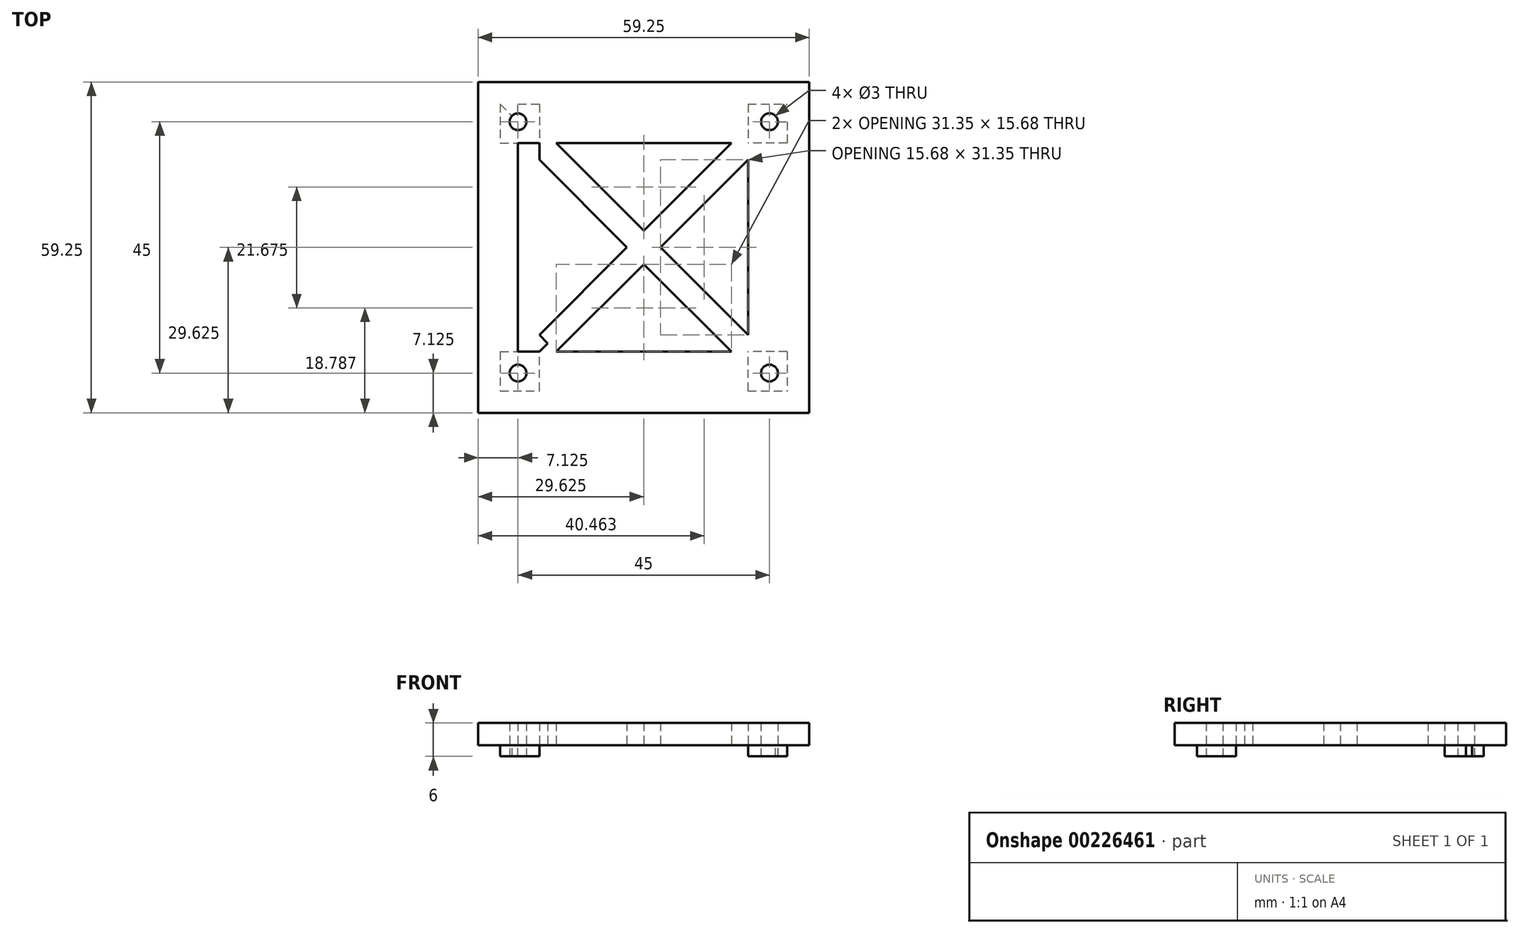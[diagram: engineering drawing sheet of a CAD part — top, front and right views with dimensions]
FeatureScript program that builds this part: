
annotation { "Feature Type Name" : "Feature", "Feature Type Description" : "" }
export const myFeature = defineFeature(function(context is Context, id is Id, definition is map)
    precondition{}
    {
        {
            var Q0;
            Q0=qCreatedBy(makeId("Top.planeOp"),FACE);
            var sketch = newSketch(context, id + "F0", { "sketchPlane" : qUnion([Q0])});
            skLineSegment(sketch, "E0.bottom", {"start": v(0, 0) * mm, "end": v(51.35, 0) * mm});
            skLineSegment(sketch, "E0.top", {"start": v(0, -51.35) * mm, "end": v(51.35, -51.35) * mm});
            skLineSegment(sketch, "E0.left", {"start": v(0, 0) * mm, "end": v(0, -51.35) * mm});
            skLineSegment(sketch, "E0.right", {"start": v(51.35, 0) * mm, "end": v(51.35, -51.35) * mm});
            skCircle(sketch, "E1", {"center": v(3.17, -3.17) * mm, "radius": 1.5 * mm});
            skCircle(sketch, "E2", {"center": v(48.17, -3.18) * mm, "radius": 1.5 * mm});
            skCircle(sketch, "E3", {"center": v(48.18, -48.17) * mm, "radius": 1.5 * mm});
            skCircle(sketch, "E4", {"center": v(3.18, -48.17) * mm, "radius": 1.5 * mm});
            skLineSegment(sketch, "E5", {"start": v(3.18, -51.35) * mm, "end": v(3.18, -48.17) * mm});
            skLineSegment(sketch, "E6", {"start": v(3.18, -48.17) * mm, "end": v(0, -48.17) * mm});
            skLineSegment(sketch, "E7", {"start": v(48.18, -48.17) * mm, "end": v(51.35, -48.17) * mm});
            skLineSegment(sketch, "E8", {"start": v(48.18, -48.17) * mm, "end": v(48.18, -51.35) * mm});
            skLineSegment(sketch, "E9", {"start": v(48.17, -3.18) * mm, "end": v(48.17, 0) * mm});
            skLineSegment(sketch, "E10", {"start": v(0, 0) * mm, "end": v(0, 0) * mm});
            skLineSegment(sketch, "E11", {"start": v(0, 0) * mm, "end": v(-3.95, 3.95) * mm});
            skLineSegment(sketch, "E12", {"start": v(51.35, 0) * mm, "end": v(55.3, 3.95) * mm});
            skLineSegment(sketch, "E13", {"start": v(51.35, -51.35) * mm, "end": v(55.3, -55.3) * mm});
            skLineSegment(sketch, "E14", {"start": v(55.3, -55.3) * mm, "end": v(-3.95, -55.3) * mm});
            skLineSegment(sketch, "E15", {"start": v(-3.95, -55.3) * mm, "end": v(0, -51.35) * mm});
            skLineSegment(sketch, "E16", {"start": v(-3.95, -55.3) * mm, "end": v(-3.95, 3.95) * mm});
            skLineSegment(sketch, "E17", {"start": v(55.3, 3.95) * mm, "end": v(-3.95, 3.95) * mm});
            skLineSegment(sketch, "E18", {"start": v(55.3, 3.95) * mm, "end": v(55.3, -55.3) * mm});
            skLineSegment(sketch, "E19.bottom", {"start": v(0, -51.35) * mm, "end": v(7, -51.35) * mm});
            skLineSegment(sketch, "E19.top", {"start": v(0, -44.35) * mm, "end": v(7, -44.35) * mm});
            skLineSegment(sketch, "E19.left", {"start": v(0, -51.35) * mm, "end": v(0, -44.35) * mm});
            skLineSegment(sketch, "E19.right", {"start": v(7, -51.35) * mm, "end": v(7, -44.35) * mm});
            skLineSegment(sketch, "E20.bottom", {"start": v(51.35, -51.35) * mm, "end": v(44.35, -51.35) * mm});
            skLineSegment(sketch, "E20.top", {"start": v(51.35, -44.35) * mm, "end": v(44.35, -44.35) * mm});
            skLineSegment(sketch, "E20.left", {"start": v(51.35, -51.35) * mm, "end": v(51.35, -44.35) * mm});
            skLineSegment(sketch, "E20.right", {"start": v(44.35, -51.35) * mm, "end": v(44.35, -44.35) * mm});
            skLineSegment(sketch, "E21.bottom", {"start": v(51.35, 0) * mm, "end": v(44.35, 0) * mm});
            skLineSegment(sketch, "E21.top", {"start": v(51.35, -7) * mm, "end": v(44.35, -7) * mm});
            skLineSegment(sketch, "E21.left", {"start": v(51.35, 0) * mm, "end": v(51.35, -7) * mm});
            skLineSegment(sketch, "E21.right", {"start": v(44.35, 0) * mm, "end": v(44.35, -7) * mm});
            skLineSegment(sketch, "E22.bottom", {"start": v(0, 0) * mm, "end": v(7, 0) * mm});
            skLineSegment(sketch, "E22.top", {"start": v(0, -7) * mm, "end": v(7, -7) * mm});
            skLineSegment(sketch, "E22.left", {"start": v(0, 0) * mm, "end": v(0, -7) * mm});
            skLineSegment(sketch, "E22.right", {"start": v(7, 0) * mm, "end": v(7, -7) * mm});
            skLineSegment(sketch, "E23", {"start": v(7, -44.35) * mm, "end": v(7, -7) * mm});
            skLineSegment(sketch, "E24", {"start": v(44.35, -7) * mm, "end": v(7, -7) * mm});
            skLineSegment(sketch, "E25", {"start": v(44.35, -7) * mm, "end": v(44.35, -44.35) * mm});
            skLineSegment(sketch, "E26", {"start": v(44.35, -44.35) * mm, "end": v(7, -44.35) * mm});
            skLineSegment(sketch, "E27", {"start": v(7, -44.35) * mm, "end": v(44.35, -7) * mm});
            skLineSegment(sketch, "E28", {"start": v(44.35, -44.35) * mm, "end": v(7, -7) * mm});
            skLineSegment(sketch, "E29", {"start": v(10, -44.35) * mm, "end": v(44.35, -10) * mm});
            skLineSegment(sketch, "E30", {"start": v(44.35, -10) * mm, "end": v(41.35, -7) * mm});
            skLineSegment(sketch, "E31", {"start": v(41.35, -7) * mm, "end": v(7, -41.35) * mm});
            skLineSegment(sketch, "E32", {"start": v(7, -10) * mm, "end": v(41.35, -44.35) * mm});
            skLineSegment(sketch, "E33", {"start": v(41.35, -44.35) * mm, "end": v(44.35, -41.35) * mm});
            skLineSegment(sketch, "E34", {"start": v(44.35, -41.35) * mm, "end": v(10, -7) * mm});
            skLineSegment(sketch, "E35", {"start": v(10, -7) * mm, "end": v(7, -10) * mm});
            skLineSegment(sketch, "E36", {"start": v(7, -41.35) * mm, "end": v(10, -44.35) * mm});
            skLineSegment(sketch, "E37", {"start": v(42.85, -8.5) * mm, "end": v(41.35, -7) * mm});
            skLineSegment(sketch, "E38", {"start": v(7, -41.35) * mm, "end": v(7, -44.35) * mm});
            skLineSegment(sketch, "E39", {"start": v(0, -51.35) * mm, "end": v(7, -44.35) * mm});
            skLineSegment(sketch, "E40", {"start": v(0, 0) * mm, "end": v(7, -7) * mm});
            skLineSegment(sketch, "E41", {"start": v(51.35, 0) * mm, "end": v(44.35, -7) * mm});
            skLineSegment(sketch, "E42", {"start": v(44.35, -44.35) * mm, "end": v(51.35, -51.35) * mm});
            skLineSegment(sketch, "E43", {"start": v(48.17, -3.18) * mm, "end": v(51.35, -3.18) * mm});
            skLineSegment(sketch, "E44", {"start": v(3.17, -3.17) * mm, "end": v(0, -3.17) * mm});
            skLineSegment(sketch, "E45", {"start": v(3.17, -3.17) * mm, "end": v(3.17, 0) * mm});
            skLineSegment(sketch, "E46", {"start": v(3.18, -48.17) * mm, "end": v(48.18, -48.17) * mm});
            skLineSegment(sketch, "E47", {"start": v(48.17, -48.17) * mm, "end": v(48.17, -3.18) * mm});
            skLineSegment(sketch, "E48", {"start": v(48.17, -3.18) * mm, "end": v(3.18, -3.17) * mm});
            skLineSegment(sketch, "E49", {"start": v(3.17, -3.18) * mm, "end": v(3.18, -48.17) * mm});
            skSolve(sketch);
        }
        {
            var Q0;
            {var subQ2=sQuery(id+"F0.wireOp",EDGE,"E0.top");Q0=makeQuery(id+"F0.imprint","IMPRINT",FACE,{"disambiguationData":[TD([[makeQuery(id+"F0.imprint","IMPRINT",EDGE,{"derivedFrom":subQ2}),-1.0]])]});}
            var Q1;
            Q1=makeQuery(id+"F0.imprint","IMPRINT",FACE,{"disambiguationData":[TD([[makeQuery(id+"F0.imprint","IMPRINT",EDGE,{"derivedFrom":sQuery(id+"F0.wireOp",EDGE,"E0.left")}),1.0]])]});
            var Q2;
            Q2=makeQuery(id+"F0.imprint","IMPRINT",FACE,{"disambiguationData":[TD([[makeQuery(id+"F0.imprint","IMPRINT",EDGE,{"derivedFrom":sQuery(id+"F0.wireOp",EDGE,"E0.top")}),1.0]])]});
            var Q3;
            {var subQ9=sQuery(id+"F0.wireOp",EDGE,"E19.top");Q3=makeQuery(id+"F0.imprint","IMPRINT",FACE,{"disambiguationData":[TD([[makeQuery(id+"F0.imprint","IMPRINT",EDGE,{"derivedFrom":subQ9}),-1.0]])]});}
            var Q4;
            {var subQ1=sQuery(id+"F0.wireOp",EDGE,"E5");var subQ7=sQuery(id+"F0.wireOp",EDGE,"E4");var subQ9=makeQuery(id+"F0.imprint","INTERSECT",VERTEX,{"derivedFrom":[subQ7,subQ1]});Q4=makeQuery(id+"F0.imprint","IMPRINT",FACE,{"disambiguationData":[TD([[makeQuery(id+"F0.imprint","IMPRINT",EDGE,{"disambiguationData":[TD([[subQ9,1.0]])],"derivedFrom":subQ7}),-1.0]])]});}
            var Q5;
            {var subQ1=sQuery(id+"F0.wireOp",EDGE,"E0.left");Q5=makeQuery(id+"F0.imprint","IMPRINT",FACE,{"disambiguationData":[TD([[makeQuery(id+"F0.imprint","IMPRINT",EDGE,{"derivedFrom":subQ1}),-1.0]])]});}
            var Q6;
            {var subQ4=sQuery(id+"F0.wireOp",EDGE,"Czqd3Wxc-25fJ-mDIk-frtU-pVyHBjyavdYw");Q6=makeQuery(id+"F0.imprint","IMPRINT",FACE,{"disambiguationData":[TD([[makeQuery(id+"F0.imprint","IMPRINT",EDGE,{"derivedFrom":subQ4}),-1.0]])]});}
            var Q7;
            {var subQ0=sQuery(id+"F0.wireOp",EDGE,"nTWrYmdF-bnnp-oIgE-1onG-Oaq0rmlScgZV");Q7=makeQuery(id+"F0.imprint","IMPRINT",FACE,{"disambiguationData":[TD([[makeQuery(id+"F0.imprint","IMPRINT",EDGE,{"derivedFrom":subQ0}),1.0]])]});}
            var Q8;
            {var subQ0=sQuery(id+"F0.wireOp",EDGE,"Czqd3Wxc-25fJ-mDIk-frtU-pVyHBjyavdYw");Q8=makeQuery(id+"F0.imprint","IMPRINT",FACE,{"disambiguationData":[TD([[makeQuery(id+"F0.imprint","IMPRINT",EDGE,{"derivedFrom":subQ0}),1.0]])]});}
            var Q9;
            {var subQ2=sQuery(id+"F0.wireOp",EDGE,"E0.bottom");Q9=makeQuery(id+"F0.imprint","IMPRINT",FACE,{"disambiguationData":[TD([[makeQuery(id+"F0.imprint","IMPRINT",EDGE,{"derivedFrom":subQ2}),1.0]])]});}
            var Q10;
            Q10=makeQuery(id+"F0.imprint","IMPRINT",FACE,{"disambiguationData":[TD([[makeQuery(id+"F0.imprint","IMPRINT",EDGE,{"derivedFrom":sQuery(id+"F0.wireOp",EDGE,"E0.bottom")}),-1.0]])]});
            var Q11;
            {var subQ4=sQuery(id+"F0.wireOp",EDGE,"JuPnyzvd-dEvb-ISZh-nlHp-12VVDodoZXJM");Q11=makeQuery(id+"F0.imprint","IMPRINT",FACE,{"disambiguationData":[TD([[makeQuery(id+"F0.imprint","IMPRINT",EDGE,{"derivedFrom":subQ4}),1.0]])]});}
            var Q12;
            {var subQ5=sQuery(id+"F0.wireOp",EDGE,"JuPnyzvd-dEvb-ISZh-nlHp-12VVDodoZXJM");Q12=makeQuery(id+"F0.imprint","IMPRINT",FACE,{"disambiguationData":[TD([[makeQuery(id+"F0.imprint","IMPRINT",EDGE,{"derivedFrom":subQ5}),-1.0]])]});}
            var Q13;
            {var subQ4=sQuery(id+"F0.wireOp",EDGE,"E0.right");Q13=makeQuery(id+"F0.imprint","IMPRINT",FACE,{"disambiguationData":[TD([[makeQuery(id+"F0.imprint","IMPRINT",EDGE,{"derivedFrom":subQ4}),1.0]])]});}
            var Q14;
            Q14=makeQuery(id+"F0.imprint","IMPRINT",FACE,{"disambiguationData":[TD([[makeQuery(id+"F0.imprint","IMPRINT",EDGE,{"derivedFrom":sQuery(id+"F0.wireOp",EDGE,"E0.right")}),-1.0]])]});
            var Q15;
            {var subQ3=sQuery(id+"F0.wireOp",EDGE,"E3");var subQ7=sQuery(id+"F0.wireOp",EDGE,"E7");var subQ9=makeQuery(id+"F0.imprint","INTERSECT",VERTEX,{"derivedFrom":[subQ3,subQ7]});Q15=makeQuery(id+"F0.imprint","IMPRINT",FACE,{"disambiguationData":[TD([[makeQuery(id+"F0.imprint","IMPRINT",EDGE,{"disambiguationData":[TD([[subQ9,1.0]])],"derivedFrom":subQ3}),-1.0]])]});}
            var Q16;
            {var subQ10=sQuery(id+"F0.wireOp",EDGE,"E20.top");Q16=makeQuery(id+"F0.imprint","IMPRINT",FACE,{"disambiguationData":[TD([[makeQuery(id+"F0.imprint","IMPRINT",EDGE,{"derivedFrom":subQ10}),1.0]])]});}
            var Q17;
            {var subQ0=sQuery(id+"F0.wireOp",EDGE,"E38");Q17=makeQuery(id+"F0.imprint","IMPRINT",FACE,{"disambiguationData":[TD([[makeQuery(id+"F0.imprint","IMPRINT",EDGE,{"derivedFrom":subQ0}),1.0]])]});}
            var Q18;
            {var subQ0=sQuery(id+"F0.wireOp",EDGE,"E27");var subQ3=sQuery(id+"F0.wireOp",EDGE,"E36");var subQ5=makeQuery(id+"F0.imprint","INTERSECT",VERTEX,{"derivedFrom":[subQ0,subQ3]});Q18=makeQuery(id+"F0.imprint","IMPRINT",FACE,{"disambiguationData":[TD([[makeQuery(id+"F0.imprint","IMPRINT",EDGE,{"disambiguationData":[TD([[subQ5,-1.0]])],"derivedFrom":subQ3}),-1.0]])]});}
            var Q19;
            {var subQ0=sQuery(id+"F0.wireOp",EDGE,"E36");var subQ1=sQuery(id+"F0.wireOp",EDGE,"E27");var subQ2=makeQuery(id+"F0.imprint","INTERSECT",VERTEX,{"derivedFrom":[subQ1,subQ0]});Q19=makeQuery(id+"F0.imprint","IMPRINT",FACE,{"disambiguationData":[TD([[makeQuery(id+"F0.imprint","IMPRINT",EDGE,{"disambiguationData":[TD([[subQ2,-1.0]])],"derivedFrom":subQ1}),-1.0]])]});}
            var Q20;
            {var subQ0=sQuery(id+"F0.wireOp",EDGE,"E36");var subQ1=sQuery(id+"F0.wireOp",EDGE,"E27");var subQ2=makeQuery(id+"F0.imprint","INTERSECT",VERTEX,{"derivedFrom":[subQ1,subQ0]});Q20=makeQuery(id+"F0.imprint","IMPRINT",FACE,{"disambiguationData":[TD([[makeQuery(id+"F0.imprint","IMPRINT",EDGE,{"disambiguationData":[TD([[subQ2,-1.0]])],"derivedFrom":subQ1}),1.0]])]});}
            var Q21;
            {var subQ0=sQuery(id+"F0.wireOp",EDGE,"E31");var subQ1=sQuery(id+"F0.wireOp",EDGE,"E28");var subQ2=makeQuery(id+"F0.imprint","INTERSECT",VERTEX,{"derivedFrom":[subQ1,subQ0]});Q21=makeQuery(id+"F0.imprint","IMPRINT",FACE,{"disambiguationData":[TD([[makeQuery(id+"F0.imprint","IMPRINT",EDGE,{"disambiguationData":[TD([[subQ2,-1.0]])],"derivedFrom":subQ1}),1.0]])]});}
            var Q22;
            {var subQ0=sQuery(id+"F0.wireOp",EDGE,"E31");var subQ1=sQuery(id+"F0.wireOp",EDGE,"E28");var subQ2=makeQuery(id+"F0.imprint","INTERSECT",VERTEX,{"derivedFrom":[subQ1,subQ0]});Q22=makeQuery(id+"F0.imprint","IMPRINT",FACE,{"disambiguationData":[TD([[makeQuery(id+"F0.imprint","IMPRINT",EDGE,{"disambiguationData":[TD([[subQ2,-1.0]])],"derivedFrom":subQ1}),-1.0]])]});}
            var Q23;
            {var subQ0=sQuery(id+"F0.wireOp",EDGE,"E28");var subQ1=sQuery(id+"F0.wireOp",EDGE,"E27");var subQ2=makeQuery(id+"F0.imprint","INTERSECT",VERTEX,{"derivedFrom":[subQ1,subQ0]});Q23=makeQuery(id+"F0.imprint","IMPRINT",FACE,{"disambiguationData":[TD([[makeQuery(id+"F0.imprint","IMPRINT",EDGE,{"disambiguationData":[TD([[subQ2,-1.0]])],"derivedFrom":subQ1}),1.0]])]});}
            var Q24;
            {var subQ0=sQuery(id+"F0.wireOp",EDGE,"E28");var subQ1=sQuery(id+"F0.wireOp",EDGE,"E27");var subQ2=makeQuery(id+"F0.imprint","INTERSECT",VERTEX,{"derivedFrom":[subQ1,subQ0]});Q24=makeQuery(id+"F0.imprint","IMPRINT",FACE,{"disambiguationData":[TD([[makeQuery(id+"F0.imprint","IMPRINT",EDGE,{"disambiguationData":[TD([[subQ2,-1.0]])],"derivedFrom":subQ1}),-1.0]])]});}
            var Q25;
            {var subQ0=sQuery(id+"F0.wireOp",EDGE,"E32");var subQ1=sQuery(id+"F0.wireOp",EDGE,"E27");var subQ2=makeQuery(id+"F0.imprint","INTERSECT",VERTEX,{"derivedFrom":[subQ1,subQ0]});Q25=makeQuery(id+"F0.imprint","IMPRINT",FACE,{"disambiguationData":[TD([[makeQuery(id+"F0.imprint","IMPRINT",EDGE,{"disambiguationData":[TD([[subQ2,-1.0]])],"derivedFrom":subQ1}),-1.0]])]});}
            var Q26;
            {var subQ0=sQuery(id+"F0.wireOp",EDGE,"E32");var subQ1=sQuery(id+"F0.wireOp",EDGE,"E27");var subQ2=makeQuery(id+"F0.imprint","INTERSECT",VERTEX,{"derivedFrom":[subQ1,subQ0]});Q26=makeQuery(id+"F0.imprint","IMPRINT",FACE,{"disambiguationData":[TD([[makeQuery(id+"F0.imprint","IMPRINT",EDGE,{"disambiguationData":[TD([[subQ2,-1.0]])],"derivedFrom":subQ1}),1.0]])]});}
            var Q27;
            {var subQ0=sQuery(id+"F0.wireOp",EDGE,"E33");var subQ1=sQuery(id+"F0.wireOp",EDGE,"E28");var subQ2=makeQuery(id+"F0.imprint","INTERSECT",VERTEX,{"derivedFrom":[subQ1,subQ0]});Q27=makeQuery(id+"F0.imprint","IMPRINT",FACE,{"disambiguationData":[TD([[makeQuery(id+"F0.imprint","IMPRINT",EDGE,{"disambiguationData":[TD([[subQ2,-1.0]])],"derivedFrom":subQ1}),1.0]])]});}
            var Q28;
            {var subQ0=sQuery(id+"F0.wireOp",EDGE,"E33");var subQ1=sQuery(id+"F0.wireOp",EDGE,"E28");var subQ2=makeQuery(id+"F0.imprint","INTERSECT",VERTEX,{"derivedFrom":[subQ1,subQ0]});Q28=makeQuery(id+"F0.imprint","IMPRINT",FACE,{"disambiguationData":[TD([[makeQuery(id+"F0.imprint","IMPRINT",EDGE,{"disambiguationData":[TD([[subQ2,-1.0]])],"derivedFrom":subQ1}),-1.0]])]});}
            var Q29;
            {var subQ0=sQuery(id+"F0.wireOp",EDGE,"E28");var subQ3=sQuery(id+"F0.wireOp",EDGE,"E35");var subQ5=makeQuery(id+"F0.imprint","INTERSECT",VERTEX,{"derivedFrom":[subQ0,subQ3]});Q29=makeQuery(id+"F0.imprint","IMPRINT",FACE,{"disambiguationData":[TD([[makeQuery(id+"F0.imprint","IMPRINT",EDGE,{"disambiguationData":[TD([[subQ5,-1.0]])],"derivedFrom":subQ3}),-1.0]])]});}
            var Q30;
            {var subQ0=sQuery(id+"F0.wireOp",EDGE,"E28");var subQ3=sQuery(id+"F0.wireOp",EDGE,"E35");var subQ5=makeQuery(id+"F0.imprint","INTERSECT",VERTEX,{"derivedFrom":[subQ0,subQ3]});Q30=makeQuery(id+"F0.imprint","IMPRINT",FACE,{"disambiguationData":[TD([[makeQuery(id+"F0.imprint","IMPRINT",EDGE,{"disambiguationData":[TD([[subQ5,1.0]])],"derivedFrom":subQ3}),-1.0]])]});}
            var Q31;
            {var subQ0=sQuery(id+"F0.wireOp",EDGE,"E30");Q31=makeQuery(id+"F0.imprint","IMPRINT",FACE,{"disambiguationData":[TD([[makeQuery(id+"F0.imprint","IMPRINT",EDGE,{"derivedFrom":subQ0}),1.0]])]});}
            var Q32;
            {var subQ0=sQuery(id+"F0.wireOp",EDGE,"E37");Q32=makeQuery(id+"F0.imprint","IMPRINT",FACE,{"disambiguationData":[TD([[makeQuery(id+"F0.imprint","IMPRINT",EDGE,{"derivedFrom":subQ0}),1.0]])]});}
            var Q33;
            {var subQ3=sQuery(id+"F0.wireOp",EDGE,"E30");Q33=makeQuery(id+"F0.imprint","IMPRINT",FACE,{"disambiguationData":[TD([[makeQuery(id+"F0.imprint","IMPRINT",EDGE,{"derivedFrom":subQ3}),-1.0]])]});}
            var Q34;
            {var subQ0=sQuery(id+"F0.wireOp",EDGE,"E28");var subQ3=sQuery(id+"F0.wireOp",EDGE,"E33");var subQ5=makeQuery(id+"F0.imprint","INTERSECT",VERTEX,{"derivedFrom":[subQ0,subQ3]});Q34=makeQuery(id+"F0.imprint","IMPRINT",FACE,{"disambiguationData":[TD([[makeQuery(id+"F0.imprint","IMPRINT",EDGE,{"disambiguationData":[TD([[subQ5,-1.0]])],"derivedFrom":subQ3}),-1.0]])]});}
            var Q35;
            {var subQ0=sQuery(id+"F0.wireOp",EDGE,"E28");var subQ3=sQuery(id+"F0.wireOp",EDGE,"E33");var subQ5=makeQuery(id+"F0.imprint","INTERSECT",VERTEX,{"derivedFrom":[subQ0,subQ3]});Q35=makeQuery(id+"F0.imprint","IMPRINT",FACE,{"disambiguationData":[TD([[makeQuery(id+"F0.imprint","IMPRINT",EDGE,{"disambiguationData":[TD([[subQ5,1.0]])],"derivedFrom":subQ3}),-1.0]])]});}
            var Q36;
            {var subQ3=sQuery(id+"F0.wireOp",EDGE,"E37");Q36=makeQuery(id+"F0.imprint","IMPRINT",FACE,{"disambiguationData":[TD([[makeQuery(id+"F0.imprint","IMPRINT",EDGE,{"derivedFrom":subQ3}),-1.0]])]});}
            var Q37;
            {var subQ0=sQuery(id+"F0.wireOp",EDGE,"E6");var subQ1=sQuery(id+"F0.wireOp",EDGE,"E4");var subQ2=makeQuery(id+"F0.imprint","INTERSECT",VERTEX,{"derivedFrom":[subQ1,subQ0]});Q37=makeQuery(id+"F0.imprint","IMPRINT",FACE,{"disambiguationData":[TD([[makeQuery(id+"F0.imprint","IMPRINT",EDGE,{"disambiguationData":[TD([[subQ2,-1.0]])],"derivedFrom":subQ1}),-1.0]])]});}
            var Q38;
            {var subQ0=sQuery(id+"F0.wireOp",EDGE,"E19.right");Q38=makeQuery(id+"F0.imprint","IMPRINT",FACE,{"disambiguationData":[TD([[makeQuery(id+"F0.imprint","IMPRINT",EDGE,{"derivedFrom":subQ0}),1.0]])]});}
            var Q39;
            {var subQ0=sQuery(id+"F0.wireOp",EDGE,"E20.right");Q39=makeQuery(id+"F0.imprint","IMPRINT",FACE,{"disambiguationData":[TD([[makeQuery(id+"F0.imprint","IMPRINT",EDGE,{"derivedFrom":subQ0}),-1.0]])]});}
            var Q40;
            {var subQ0=sQuery(id+"F0.wireOp",EDGE,"E8");var subQ1=sQuery(id+"F0.wireOp",EDGE,"E3");var subQ2=makeQuery(id+"F0.imprint","INTERSECT",VERTEX,{"derivedFrom":[subQ1,subQ0]});Q40=makeQuery(id+"F0.imprint","IMPRINT",FACE,{"disambiguationData":[TD([[makeQuery(id+"F0.imprint","IMPRINT",EDGE,{"disambiguationData":[TD([[subQ2,-1.0]])],"derivedFrom":subQ1}),-1.0]])]});}
            var Q41;
            {var subQ0=sQuery(id+"F0.wireOp",EDGE,"E21.right");Q41=makeQuery(id+"F0.imprint","IMPRINT",FACE,{"disambiguationData":[TD([[makeQuery(id+"F0.imprint","IMPRINT",EDGE,{"derivedFrom":subQ0}),1.0]])]});}
            var Q42;
            {var subQ0=sQuery(id+"F0.wireOp",EDGE,"E41");var subQ1=sQuery(id+"F0.wireOp",EDGE,"E2");var subQ2=makeQuery(id+"F0.imprint","INTERSECT",VERTEX,{"disambiguationData":[OD(0.0)],"derivedFrom":[subQ1,subQ0]});Q42=makeQuery(id+"F0.imprint","IMPRINT",FACE,{"disambiguationData":[TD([[makeQuery(id+"F0.imprint","IMPRINT",EDGE,{"disambiguationData":[TD([[subQ2,-1.0]])],"derivedFrom":subQ1}),-1.0]])]});}
            var Q43;
            {var subQ2=sQuery(id+"F0.wireOp",EDGE,"nTWrYmdF-bnnp-oIgE-1onG-Oaq0rmlScgZV");Q43=makeQuery(id+"F0.imprint","IMPRINT",FACE,{"disambiguationData":[TD([[makeQuery(id+"F0.imprint","IMPRINT",EDGE,{"derivedFrom":subQ2}),-1.0]])]});}
            var Q44;
            {var subQ5=sQuery(id+"F0.wireOp",EDGE,"E4");var subQ7=sQuery(id+"F0.wireOp",EDGE,"E49");var subQ9=makeQuery(id+"F0.imprint","INTERSECT",VERTEX,{"derivedFrom":[subQ5,subQ7]});Q44=makeQuery(id+"F0.imprint","IMPRINT",FACE,{"disambiguationData":[TD([[makeQuery(id+"F0.imprint","IMPRINT",EDGE,{"disambiguationData":[TD([[subQ9,-1.0]])],"derivedFrom":subQ5}),-1.0]])]});}
            var Q45;
            {var subQ5=sQuery(id+"F0.wireOp",EDGE,"E5");var subQ7=sQuery(id+"F0.wireOp",EDGE,"E4");var subQ8=makeQuery(id+"F0.imprint","INTERSECT",VERTEX,{"derivedFrom":[subQ7,subQ5]});Q45=makeQuery(id+"F0.imprint","IMPRINT",FACE,{"disambiguationData":[TD([[makeQuery(id+"F0.imprint","IMPRINT",EDGE,{"disambiguationData":[TD([[subQ8,-1.0]])],"derivedFrom":subQ7}),-1.0]])]});}
            var Q46;
            {var subQ0=sQuery(id+"F0.wireOp",EDGE,"E45");var subQ3=sQuery(id+"F0.wireOp",EDGE,"E1");var subQ4=makeQuery(id+"F0.imprint","INTERSECT",VERTEX,{"derivedFrom":[subQ3,subQ0]});Q46=makeQuery(id+"F0.imprint","IMPRINT",FACE,{"disambiguationData":[TD([[makeQuery(id+"F0.imprint","IMPRINT",EDGE,{"disambiguationData":[TD([[subQ4,1.0]])],"derivedFrom":subQ3}),-1.0]])]});}
            var Q47;
            {var subQ0=sQuery(id+"F0.wireOp",EDGE,"E40");var subQ1=sQuery(id+"F0.wireOp",EDGE,"E1");var subQ2=makeQuery(id+"F0.imprint","INTERSECT",VERTEX,{"disambiguationData":[OD(1.0)],"derivedFrom":[subQ1,subQ0]});Q47=makeQuery(id+"F0.imprint","IMPRINT",FACE,{"disambiguationData":[TD([[makeQuery(id+"F0.imprint","IMPRINT",EDGE,{"disambiguationData":[TD([[subQ2,-1.0]])],"derivedFrom":subQ1}),-1.0]])]});}
            var Q48;
            {var subQ0=sQuery(id+"F0.wireOp",EDGE,"E49");var subQ1=sQuery(id+"F0.wireOp",EDGE,"E1");var subQ2=makeQuery(id+"F0.imprint","INTERSECT",VERTEX,{"derivedFrom":[subQ1,subQ0]});Q48=makeQuery(id+"F0.imprint","IMPRINT",FACE,{"disambiguationData":[TD([[makeQuery(id+"F0.imprint","IMPRINT",EDGE,{"disambiguationData":[TD([[subQ2,-1.0]])],"derivedFrom":subQ1}),-1.0]])]});}
            var Q49;
            {var subQ0=sQuery(id+"F0.wireOp",EDGE,"E44");var subQ3=sQuery(id+"F0.wireOp",EDGE,"E1");var subQ4=makeQuery(id+"F0.imprint","INTERSECT",VERTEX,{"derivedFrom":[subQ3,subQ0]});Q49=makeQuery(id+"F0.imprint","IMPRINT",FACE,{"disambiguationData":[TD([[makeQuery(id+"F0.imprint","IMPRINT",EDGE,{"disambiguationData":[TD([[subQ4,-1.0]])],"derivedFrom":subQ3}),-1.0]])]});}
            var Q50;
            {var subQ0=sQuery(id+"F0.wireOp",EDGE,"E40");var subQ1=sQuery(id+"F0.wireOp",EDGE,"E1");var subQ2=makeQuery(id+"F0.imprint","INTERSECT",VERTEX,{"disambiguationData":[OD(0.0)],"derivedFrom":[subQ1,subQ0]});Q50=makeQuery(id+"F0.imprint","IMPRINT",FACE,{"disambiguationData":[TD([[makeQuery(id+"F0.imprint","IMPRINT",EDGE,{"disambiguationData":[TD([[subQ2,-1.0]])],"derivedFrom":subQ1}),-1.0]])]});}
            var Q51;
            {var subQ3=sQuery(id+"F0.wireOp",EDGE,"E21.right");var subQ5=sQuery(id+"F0.wireOp",EDGE,"E48");var subQ6=makeQuery(id+"F0.imprint","INTERSECT",VERTEX,{"derivedFrom":[subQ3,subQ5]});Q51=makeQuery(id+"F0.imprint","IMPRINT",FACE,{"disambiguationData":[TD([[makeQuery(id+"F0.imprint","IMPRINT",EDGE,{"disambiguationData":[TD([[subQ6,-1.0]])],"derivedFrom":subQ5}),1.0]])]});}
            var Q52;
            {var subQ0=sQuery(id+"F0.wireOp",EDGE,"E38");Q52=makeQuery(id+"F0.imprint","IMPRINT",FACE,{"disambiguationData":[TD([[makeQuery(id+"F0.imprint","IMPRINT",EDGE,{"derivedFrom":subQ0}),-1.0]])]});}
            var Q53;
            {var subQ5=sQuery(id+"F0.wireOp",EDGE,"E9");var subQ7=sQuery(id+"F0.wireOp",EDGE,"E2");var subQ8=makeQuery(id+"F0.imprint","INTERSECT",VERTEX,{"derivedFrom":[subQ7,subQ5]});Q53=makeQuery(id+"F0.imprint","IMPRINT",FACE,{"disambiguationData":[TD([[makeQuery(id+"F0.imprint","IMPRINT",EDGE,{"disambiguationData":[TD([[subQ8,-1.0]])],"derivedFrom":subQ7}),-1.0]])]});}
            var Q54;
            {var subQ0=sQuery(id+"F0.wireOp",EDGE,"E41");var subQ1=sQuery(id+"F0.wireOp",EDGE,"E2");var subQ2=makeQuery(id+"F0.imprint","INTERSECT",VERTEX,{"disambiguationData":[OD(0.0)],"derivedFrom":[subQ1,subQ0]});Q54=makeQuery(id+"F0.imprint","IMPRINT",FACE,{"disambiguationData":[TD([[makeQuery(id+"F0.imprint","IMPRINT",EDGE,{"disambiguationData":[TD([[subQ2,1.0]])],"derivedFrom":subQ1}),-1.0]])]});}
            var Q55;
            {var subQ0=sQuery(id+"F0.wireOp",EDGE,"E43");var subQ3=sQuery(id+"F0.wireOp",EDGE,"E2");var subQ4=makeQuery(id+"F0.imprint","INTERSECT",VERTEX,{"derivedFrom":[subQ3,subQ0]});Q55=makeQuery(id+"F0.imprint","IMPRINT",FACE,{"disambiguationData":[TD([[makeQuery(id+"F0.imprint","IMPRINT",EDGE,{"disambiguationData":[TD([[subQ4,1.0]])],"derivedFrom":subQ3}),-1.0]])]});}
            var Q56;
            {var subQ0=sQuery(id+"F0.wireOp",EDGE,"E41");var subQ1=sQuery(id+"F0.wireOp",EDGE,"E2");var subQ2=makeQuery(id+"F0.imprint","INTERSECT",VERTEX,{"disambiguationData":[OD(1.0)],"derivedFrom":[subQ1,subQ0]});Q56=makeQuery(id+"F0.imprint","IMPRINT",FACE,{"disambiguationData":[TD([[makeQuery(id+"F0.imprint","IMPRINT",EDGE,{"disambiguationData":[TD([[subQ2,-1.0]])],"derivedFrom":subQ1}),-1.0]])]});}
            var Q57;
            {var subQ5=sQuery(id+"F0.wireOp",EDGE,"E47");var subQ7=sQuery(id+"F0.wireOp",EDGE,"E20.top");var subQ9=makeQuery(id+"F0.imprint","INTERSECT",VERTEX,{"derivedFrom":[subQ7,subQ5]});Q57=makeQuery(id+"F0.imprint","IMPRINT",FACE,{"disambiguationData":[TD([[makeQuery(id+"F0.imprint","IMPRINT",EDGE,{"disambiguationData":[TD([[subQ9,-1.0]])],"derivedFrom":subQ5}),1.0]])]});}
            var Q58;
            {var subQ5=sQuery(id+"F0.wireOp",EDGE,"E3");var subQ7=sQuery(id+"F0.wireOp",EDGE,"E47");var subQ8=makeQuery(id+"F0.imprint","INTERSECT",VERTEX,{"derivedFrom":[subQ5,subQ7]});Q58=makeQuery(id+"F0.imprint","IMPRINT",FACE,{"disambiguationData":[TD([[makeQuery(id+"F0.imprint","IMPRINT",EDGE,{"disambiguationData":[TD([[subQ8,1.0]])],"derivedFrom":subQ5}),-1.0]])]});}
            var Q59;
            {var subQ3=sQuery(id+"F0.wireOp",EDGE,"E46");var subQ7=sQuery(id+"F0.wireOp",EDGE,"E3");var subQ9=makeQuery(id+"F0.imprint","INTERSECT",VERTEX,{"derivedFrom":[subQ7,subQ3]});Q59=makeQuery(id+"F0.imprint","IMPRINT",FACE,{"disambiguationData":[TD([[makeQuery(id+"F0.imprint","IMPRINT",EDGE,{"disambiguationData":[TD([[subQ9,-1.0]])],"derivedFrom":subQ7}),-1.0]])]});}
            var Q60;
            {var subQ5=sQuery(id+"F0.wireOp",EDGE,"E19.right");var subQ7=sQuery(id+"F0.wireOp",EDGE,"E46");var subQ8=makeQuery(id+"F0.imprint","INTERSECT",VERTEX,{"derivedFrom":[subQ5,subQ7]});Q60=makeQuery(id+"F0.imprint","IMPRINT",FACE,{"disambiguationData":[TD([[makeQuery(id+"F0.imprint","IMPRINT",EDGE,{"disambiguationData":[TD([[subQ8,-1.0]])],"derivedFrom":subQ7}),1.0]])]});}
            var Q61;
            {var subQ0=sQuery(id+"F0.wireOp",EDGE,"E40");var subQ1=sQuery(id+"F0.wireOp",EDGE,"E1");var subQ2=makeQuery(id+"F0.imprint","INTERSECT",VERTEX,{"disambiguationData":[OD(0.0)],"derivedFrom":[subQ1,subQ0]});Q61=makeQuery(id+"F0.imprint","IMPRINT",FACE,{"disambiguationData":[TD([[makeQuery(id+"F0.imprint","IMPRINT",EDGE,{"disambiguationData":[TD([[subQ2,1.0]])],"derivedFrom":subQ1}),-1.0]])]});}
            extrude(context, id + "F1", {"entities" : qUnion([Q0, Q1, Q2, Q3, Q4, Q5, Q6, Q7, Q8, Q9, Q10, Q11, Q12, Q13, Q14, Q15, Q16, Q17, Q18, Q19, Q20, Q21, Q22, Q23, Q24, Q25, Q26, Q27, Q28, Q29, Q30, Q31, Q32, Q33, Q34, Q35, Q36, Q37, Q38, Q39, Q40, Q41, Q42, Q43, Q44, Q45, Q46, Q47, Q48, Q49, Q50, Q51, Q52, Q53, Q54, Q55, Q56, Q57, Q58, Q59, Q60, Q61]), "depth" : 4 * mm});
        }
        {
            var Q0;
            {var subQ9=sQuery(id+"F0.wireOp",EDGE,"E19.top");Q0=makeQuery(id+"F0.imprint","IMPRINT",FACE,{"disambiguationData":[TD([[makeQuery(id+"F0.imprint","IMPRINT",EDGE,{"derivedFrom":subQ9}),-1.0]])]});}
            var Q1;
            {var subQ1=sQuery(id+"F0.wireOp",EDGE,"E5");var subQ7=sQuery(id+"F0.wireOp",EDGE,"E4");var subQ9=makeQuery(id+"F0.imprint","INTERSECT",VERTEX,{"derivedFrom":[subQ7,subQ1]});Q1=makeQuery(id+"F0.imprint","IMPRINT",FACE,{"disambiguationData":[TD([[makeQuery(id+"F0.imprint","IMPRINT",EDGE,{"disambiguationData":[TD([[subQ9,1.0]])],"derivedFrom":subQ7}),-1.0]])]});}
            var Q2;
            {var subQ10=sQuery(id+"F0.wireOp",EDGE,"E20.top");Q2=makeQuery(id+"F0.imprint","IMPRINT",FACE,{"disambiguationData":[TD([[makeQuery(id+"F0.imprint","IMPRINT",EDGE,{"derivedFrom":subQ10}),1.0]])]});}
            var Q3;
            {var subQ3=sQuery(id+"F0.wireOp",EDGE,"E3");var subQ7=sQuery(id+"F0.wireOp",EDGE,"E7");var subQ9=makeQuery(id+"F0.imprint","INTERSECT",VERTEX,{"derivedFrom":[subQ3,subQ7]});Q3=makeQuery(id+"F0.imprint","IMPRINT",FACE,{"disambiguationData":[TD([[makeQuery(id+"F0.imprint","IMPRINT",EDGE,{"disambiguationData":[TD([[subQ9,1.0]])],"derivedFrom":subQ3}),-1.0]])]});}
            var Q4;
            {var subQ4=sQuery(id+"F0.wireOp",EDGE,"JuPnyzvd-dEvb-ISZh-nlHp-12VVDodoZXJM");Q4=makeQuery(id+"F0.imprint","IMPRINT",FACE,{"disambiguationData":[TD([[makeQuery(id+"F0.imprint","IMPRINT",EDGE,{"derivedFrom":subQ4}),1.0]])]});}
            var Q5;
            {var subQ5=sQuery(id+"F0.wireOp",EDGE,"JuPnyzvd-dEvb-ISZh-nlHp-12VVDodoZXJM");Q5=makeQuery(id+"F0.imprint","IMPRINT",FACE,{"disambiguationData":[TD([[makeQuery(id+"F0.imprint","IMPRINT",EDGE,{"derivedFrom":subQ5}),-1.0]])]});}
            var Q6;
            {var subQ4=sQuery(id+"F0.wireOp",EDGE,"Czqd3Wxc-25fJ-mDIk-frtU-pVyHBjyavdYw");Q6=makeQuery(id+"F0.imprint","IMPRINT",FACE,{"disambiguationData":[TD([[makeQuery(id+"F0.imprint","IMPRINT",EDGE,{"derivedFrom":subQ4}),-1.0]])]});}
            var Q7;
            {var subQ0=sQuery(id+"F0.wireOp",EDGE,"Czqd3Wxc-25fJ-mDIk-frtU-pVyHBjyavdYw");Q7=makeQuery(id+"F0.imprint","IMPRINT",FACE,{"disambiguationData":[TD([[makeQuery(id+"F0.imprint","IMPRINT",EDGE,{"derivedFrom":subQ0}),1.0]])]});}
            var Q8;
            {var subQ0=sQuery(id+"F0.wireOp",EDGE,"nTWrYmdF-bnnp-oIgE-1onG-Oaq0rmlScgZV");Q8=makeQuery(id+"F0.imprint","IMPRINT",FACE,{"disambiguationData":[TD([[makeQuery(id+"F0.imprint","IMPRINT",EDGE,{"derivedFrom":subQ0}),1.0]])]});}
            var Q9;
            {var subQ0=sQuery(id+"F0.wireOp",EDGE,"E19.right");Q9=makeQuery(id+"F0.imprint","IMPRINT",FACE,{"disambiguationData":[TD([[makeQuery(id+"F0.imprint","IMPRINT",EDGE,{"derivedFrom":subQ0}),1.0]])]});}
            var Q10;
            {var subQ0=sQuery(id+"F0.wireOp",EDGE,"E6");var subQ1=sQuery(id+"F0.wireOp",EDGE,"E4");var subQ2=makeQuery(id+"F0.imprint","INTERSECT",VERTEX,{"derivedFrom":[subQ1,subQ0]});Q10=makeQuery(id+"F0.imprint","IMPRINT",FACE,{"disambiguationData":[TD([[makeQuery(id+"F0.imprint","IMPRINT",EDGE,{"disambiguationData":[TD([[subQ2,-1.0]])],"derivedFrom":subQ1}),-1.0]])]});}
            var Q11;
            {var subQ0=sQuery(id+"F0.wireOp",EDGE,"E20.right");Q11=makeQuery(id+"F0.imprint","IMPRINT",FACE,{"disambiguationData":[TD([[makeQuery(id+"F0.imprint","IMPRINT",EDGE,{"derivedFrom":subQ0}),-1.0]])]});}
            var Q12;
            {var subQ0=sQuery(id+"F0.wireOp",EDGE,"E8");var subQ1=sQuery(id+"F0.wireOp",EDGE,"E3");var subQ2=makeQuery(id+"F0.imprint","INTERSECT",VERTEX,{"derivedFrom":[subQ1,subQ0]});Q12=makeQuery(id+"F0.imprint","IMPRINT",FACE,{"disambiguationData":[TD([[makeQuery(id+"F0.imprint","IMPRINT",EDGE,{"disambiguationData":[TD([[subQ2,-1.0]])],"derivedFrom":subQ1}),-1.0]])]});}
            var Q13;
            Q13=makeQuery(id+"F1.opExtrude","SWEPT_FACE",FACE,{"disambiguationData":[OSD([sQuery(id+"F0.wireOp",EDGE,"E20.bottom")])]});
            var Q14;
            {var subQ2=sQuery(id+"F0.wireOp",EDGE,"nTWrYmdF-bnnp-oIgE-1onG-Oaq0rmlScgZV");Q14=makeQuery(id+"F0.imprint","IMPRINT",FACE,{"disambiguationData":[TD([[makeQuery(id+"F0.imprint","IMPRINT",EDGE,{"derivedFrom":subQ2}),-1.0]])]});}
            var Q15;
            {var subQ0=sQuery(id+"F0.wireOp",EDGE,"E21.right");Q15=makeQuery(id+"F0.imprint","IMPRINT",FACE,{"disambiguationData":[TD([[makeQuery(id+"F0.imprint","IMPRINT",EDGE,{"derivedFrom":subQ0}),1.0]])]});}
            var Q16;
            {var subQ0=sQuery(id+"F0.wireOp",EDGE,"E41");var subQ1=sQuery(id+"F0.wireOp",EDGE,"E2");var subQ2=makeQuery(id+"F0.imprint","INTERSECT",VERTEX,{"disambiguationData":[OD(0.0)],"derivedFrom":[subQ1,subQ0]});Q16=makeQuery(id+"F0.imprint","IMPRINT",FACE,{"disambiguationData":[TD([[makeQuery(id+"F0.imprint","IMPRINT",EDGE,{"disambiguationData":[TD([[subQ2,-1.0]])],"derivedFrom":subQ1}),-1.0]])]});}
            var Q17;
            {var subQ0=sQuery(id+"F0.wireOp",EDGE,"E44");var subQ3=sQuery(id+"F0.wireOp",EDGE,"E1");var subQ4=makeQuery(id+"F0.imprint","INTERSECT",VERTEX,{"derivedFrom":[subQ3,subQ0]});Q17=makeQuery(id+"F0.imprint","IMPRINT",FACE,{"disambiguationData":[TD([[makeQuery(id+"F0.imprint","IMPRINT",EDGE,{"disambiguationData":[TD([[subQ4,-1.0]])],"derivedFrom":subQ3}),-1.0]])]});}
            var Q18;
            {var subQ0=sQuery(id+"F0.wireOp",EDGE,"E49");var subQ1=sQuery(id+"F0.wireOp",EDGE,"E1");var subQ2=makeQuery(id+"F0.imprint","INTERSECT",VERTEX,{"derivedFrom":[subQ1,subQ0]});Q18=makeQuery(id+"F0.imprint","IMPRINT",FACE,{"disambiguationData":[TD([[makeQuery(id+"F0.imprint","IMPRINT",EDGE,{"disambiguationData":[TD([[subQ2,-1.0]])],"derivedFrom":subQ1}),-1.0]])]});}
            var Q19;
            {var subQ0=sQuery(id+"F0.wireOp",EDGE,"E40");var subQ1=sQuery(id+"F0.wireOp",EDGE,"E1");var subQ2=makeQuery(id+"F0.imprint","INTERSECT",VERTEX,{"disambiguationData":[OD(1.0)],"derivedFrom":[subQ1,subQ0]});Q19=makeQuery(id+"F0.imprint","IMPRINT",FACE,{"disambiguationData":[TD([[makeQuery(id+"F0.imprint","IMPRINT",EDGE,{"disambiguationData":[TD([[subQ2,-1.0]])],"derivedFrom":subQ1}),-1.0]])]});}
            var Q20;
            {var subQ0=sQuery(id+"F0.wireOp",EDGE,"E40");var subQ1=sQuery(id+"F0.wireOp",EDGE,"E1");var subQ2=makeQuery(id+"F0.imprint","INTERSECT",VERTEX,{"disambiguationData":[OD(0.0)],"derivedFrom":[subQ1,subQ0]});Q20=makeQuery(id+"F0.imprint","IMPRINT",FACE,{"disambiguationData":[TD([[makeQuery(id+"F0.imprint","IMPRINT",EDGE,{"disambiguationData":[TD([[subQ2,1.0]])],"derivedFrom":subQ1}),-1.0]])]});}
            var Q21;
            {var subQ0=sQuery(id+"F0.wireOp",EDGE,"E40");var subQ1=sQuery(id+"F0.wireOp",EDGE,"E1");var subQ2=makeQuery(id+"F0.imprint","INTERSECT",VERTEX,{"disambiguationData":[OD(0.0)],"derivedFrom":[subQ1,subQ0]});Q21=makeQuery(id+"F0.imprint","IMPRINT",FACE,{"disambiguationData":[TD([[makeQuery(id+"F0.imprint","IMPRINT",EDGE,{"disambiguationData":[TD([[subQ2,-1.0]])],"derivedFrom":subQ1}),-1.0]])]});}
            var Q22;
            {var subQ0=sQuery(id+"F0.wireOp",EDGE,"E45");var subQ3=sQuery(id+"F0.wireOp",EDGE,"E1");var subQ4=makeQuery(id+"F0.imprint","INTERSECT",VERTEX,{"derivedFrom":[subQ3,subQ0]});Q22=makeQuery(id+"F0.imprint","IMPRINT",FACE,{"disambiguationData":[TD([[makeQuery(id+"F0.imprint","IMPRINT",EDGE,{"disambiguationData":[TD([[subQ4,1.0]])],"derivedFrom":subQ3}),-1.0]])]});}
            var Q23;
            {var subQ5=sQuery(id+"F0.wireOp",EDGE,"E9");var subQ7=sQuery(id+"F0.wireOp",EDGE,"E2");var subQ8=makeQuery(id+"F0.imprint","INTERSECT",VERTEX,{"derivedFrom":[subQ7,subQ5]});Q23=makeQuery(id+"F0.imprint","IMPRINT",FACE,{"disambiguationData":[TD([[makeQuery(id+"F0.imprint","IMPRINT",EDGE,{"disambiguationData":[TD([[subQ8,-1.0]])],"derivedFrom":subQ7}),-1.0]])]});}
            var Q24;
            {var subQ0=sQuery(id+"F0.wireOp",EDGE,"E41");var subQ1=sQuery(id+"F0.wireOp",EDGE,"E2");var subQ2=makeQuery(id+"F0.imprint","INTERSECT",VERTEX,{"disambiguationData":[OD(0.0)],"derivedFrom":[subQ1,subQ0]});Q24=makeQuery(id+"F0.imprint","IMPRINT",FACE,{"disambiguationData":[TD([[makeQuery(id+"F0.imprint","IMPRINT",EDGE,{"disambiguationData":[TD([[subQ2,1.0]])],"derivedFrom":subQ1}),-1.0]])]});}
            var Q25;
            {var subQ0=sQuery(id+"F0.wireOp",EDGE,"E43");var subQ3=sQuery(id+"F0.wireOp",EDGE,"E2");var subQ4=makeQuery(id+"F0.imprint","INTERSECT",VERTEX,{"derivedFrom":[subQ3,subQ0]});Q25=makeQuery(id+"F0.imprint","IMPRINT",FACE,{"disambiguationData":[TD([[makeQuery(id+"F0.imprint","IMPRINT",EDGE,{"disambiguationData":[TD([[subQ4,1.0]])],"derivedFrom":subQ3}),-1.0]])]});}
            var Q26;
            {var subQ0=sQuery(id+"F0.wireOp",EDGE,"E41");var subQ1=sQuery(id+"F0.wireOp",EDGE,"E2");var subQ2=makeQuery(id+"F0.imprint","INTERSECT",VERTEX,{"disambiguationData":[OD(1.0)],"derivedFrom":[subQ1,subQ0]});Q26=makeQuery(id+"F0.imprint","IMPRINT",FACE,{"disambiguationData":[TD([[makeQuery(id+"F0.imprint","IMPRINT",EDGE,{"disambiguationData":[TD([[subQ2,-1.0]])],"derivedFrom":subQ1}),-1.0]])]});}
            var Q27;
            {var subQ5=sQuery(id+"F0.wireOp",EDGE,"E3");var subQ7=sQuery(id+"F0.wireOp",EDGE,"E47");var subQ8=makeQuery(id+"F0.imprint","INTERSECT",VERTEX,{"derivedFrom":[subQ5,subQ7]});Q27=makeQuery(id+"F0.imprint","IMPRINT",FACE,{"disambiguationData":[TD([[makeQuery(id+"F0.imprint","IMPRINT",EDGE,{"disambiguationData":[TD([[subQ8,1.0]])],"derivedFrom":subQ5}),-1.0]])]});}
            var Q28;
            {var subQ3=sQuery(id+"F0.wireOp",EDGE,"E46");var subQ7=sQuery(id+"F0.wireOp",EDGE,"E3");var subQ9=makeQuery(id+"F0.imprint","INTERSECT",VERTEX,{"derivedFrom":[subQ7,subQ3]});Q28=makeQuery(id+"F0.imprint","IMPRINT",FACE,{"disambiguationData":[TD([[makeQuery(id+"F0.imprint","IMPRINT",EDGE,{"disambiguationData":[TD([[subQ9,-1.0]])],"derivedFrom":subQ7}),-1.0]])]});}
            var Q29;
            {var subQ5=sQuery(id+"F0.wireOp",EDGE,"E5");var subQ7=sQuery(id+"F0.wireOp",EDGE,"E4");var subQ8=makeQuery(id+"F0.imprint","INTERSECT",VERTEX,{"derivedFrom":[subQ7,subQ5]});Q29=makeQuery(id+"F0.imprint","IMPRINT",FACE,{"disambiguationData":[TD([[makeQuery(id+"F0.imprint","IMPRINT",EDGE,{"disambiguationData":[TD([[subQ8,-1.0]])],"derivedFrom":subQ7}),-1.0]])]});}
            var Q30;
            {var subQ5=sQuery(id+"F0.wireOp",EDGE,"E4");var subQ7=sQuery(id+"F0.wireOp",EDGE,"E49");var subQ9=makeQuery(id+"F0.imprint","INTERSECT",VERTEX,{"derivedFrom":[subQ5,subQ7]});Q30=makeQuery(id+"F0.imprint","IMPRINT",FACE,{"disambiguationData":[TD([[makeQuery(id+"F0.imprint","IMPRINT",EDGE,{"disambiguationData":[TD([[subQ9,-1.0]])],"derivedFrom":subQ5}),-1.0]])]});}
            extrude(context, id + "F2", {"entities" : qUnion([Q0, Q1, Q2, Q3, Q4, Q5, Q6, Q7, Q8, Q9, Q10, Q11, Q12, Q13, Q14, Q15, Q16, Q17, Q18, Q19, Q20, Q21, Q22, Q23, Q24, Q25, Q26, Q27, Q28, Q29, Q30]), "operationType" : NewBodyOperationType.ADD, "oppositeDirection" : true, "depth" : 2 * mm});
        }
    });
